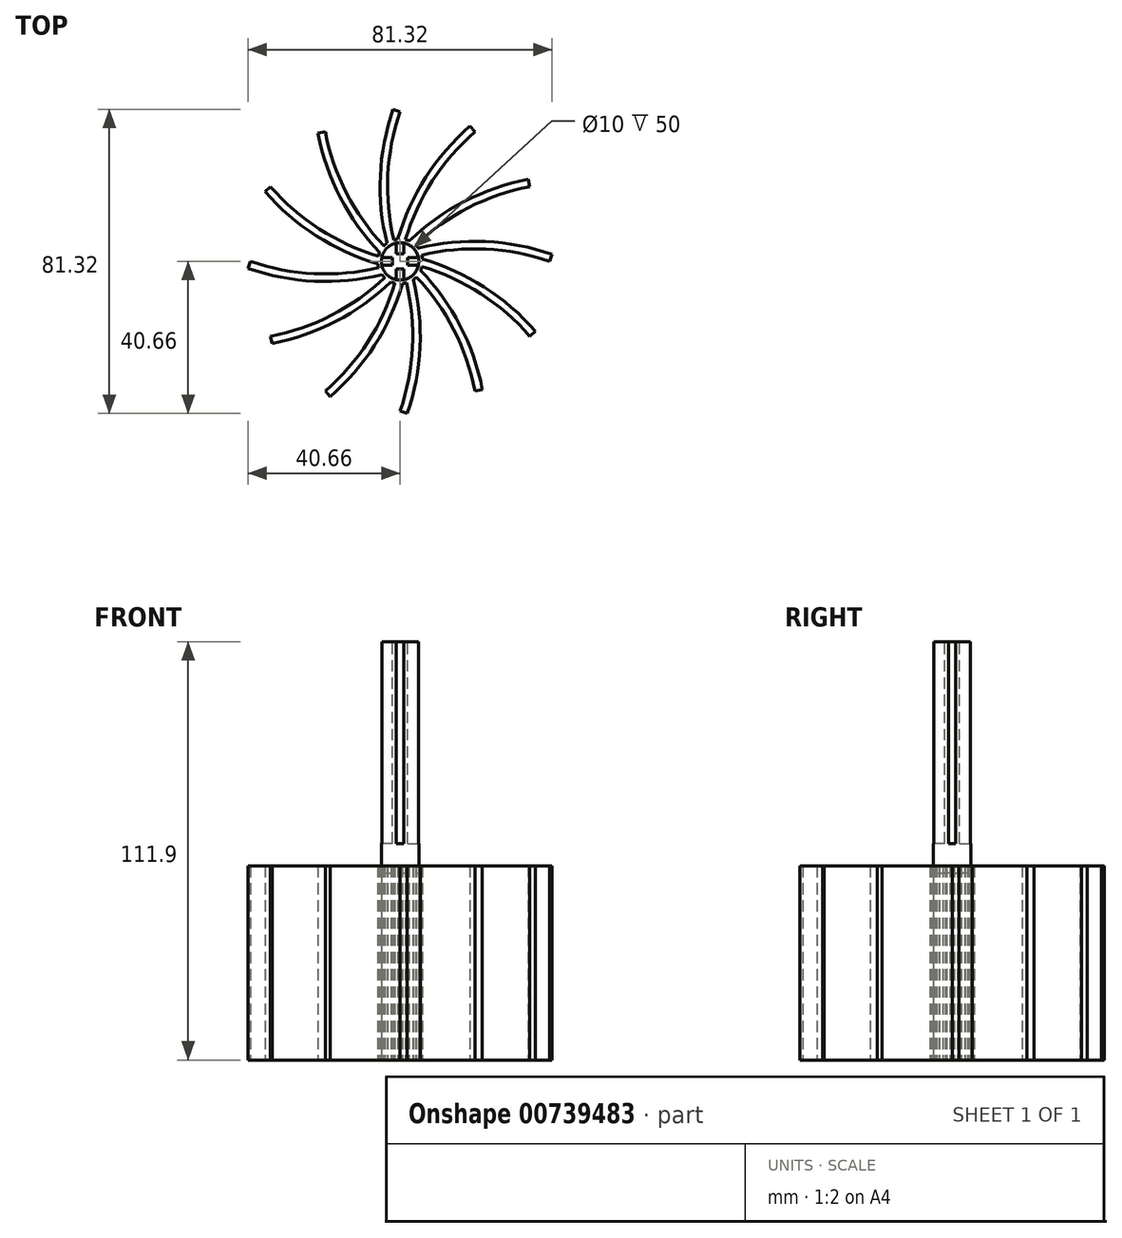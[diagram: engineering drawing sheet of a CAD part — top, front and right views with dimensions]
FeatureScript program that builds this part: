
annotation { "Feature Type Name" : "Feature", "Feature Type Description" : "" }
export const myFeature = defineFeature(function(context is Context, id is Id, definition is map)
    precondition{}
    {
        {
            var Q0;
            Q0=qCreatedBy(makeId("Top.planeOp"),FACE);
            var sketch = newSketch(context, id + "F0", { "sketchPlane" : qUnion([Q0])});
            skCircle(sketch, "E0", {"center": v(0, 0) * mm, "radius": 6 * mm});
            skArc(sketch, "E1", {"start": v(0, 40) * mm, "mid": v(-3.37, 20) * mm, "end": v(0, 0) * mm});
            skArc(sketch, "E2.1.0", {"start": v(-20, 34.64) * mm, "mid": v(-12.92, 15.64) * mm, "end": v(0, 0) * mm});
            skArc(sketch, "E2.2.0", {"start": v(-34.64, 20) * mm, "mid": v(-19, 7.08) * mm, "end": v(0, 0) * mm});
            skArc(sketch, "E2.3.0", {"start": v(-40, 0) * mm, "mid": v(-20, -3.37) * mm, "end": v(0, 0) * mm});
            skArc(sketch, "E2.4.0", {"start": v(-34.64, -20) * mm, "mid": v(-15.64, -12.92) * mm, "end": v(0, 0) * mm});
            skArc(sketch, "E2.5.0", {"start": v(-20, -34.64) * mm, "mid": v(-7.08, -19) * mm, "end": v(0, 0) * mm});
            skArc(sketch, "E2.6.0", {"start": v(0, -40) * mm, "mid": v(3.37, -20) * mm, "end": v(0, 0) * mm});
            skArc(sketch, "E2.7.0", {"start": v(20, -34.64) * mm, "mid": v(12.92, -15.64) * mm, "end": v(0, 0) * mm});
            skArc(sketch, "E2.8.0", {"start": v(34.64, -20) * mm, "mid": v(19, -7.08) * mm, "end": v(0, 0) * mm});
            skArc(sketch, "E2.9.0", {"start": v(40, 0) * mm, "mid": v(20, 3.37) * mm, "end": v(0, 0) * mm});
            skArc(sketch, "E2.10.0", {"start": v(34.64, 20) * mm, "mid": v(15.64, 12.92) * mm, "end": v(0, 0) * mm});
            skArc(sketch, "E2.11.0", {"start": v(20, 34.64) * mm, "mid": v(7.08, 19) * mm, "end": v(0, 0) * mm});
            skArc(sketch, "E3.0", {"start": v(-1.89, 40.66) * mm, "mid": v(-5.37, 20) * mm, "end": v(-1.89, -0.66) * mm});
            skArc(sketch, "E4.0", {"start": v(-21.96, 34.26) * mm, "mid": v(-14.65, 14.64) * mm, "end": v(-1.3, -1.51) * mm});
            skArc(sketch, "E5.0", {"start": v(-36.15, 18.7) * mm, "mid": v(-20, 5.35) * mm, "end": v(-0.38, -1.96) * mm});
            skArc(sketch, "E6.0", {"start": v(-40.66, -1.89) * mm, "mid": v(-20, -5.37) * mm, "end": v(0.66, -1.89) * mm});
            skArc(sketch, "E7.0", {"start": v(-34.26, -21.96) * mm, "mid": v(-14.64, -14.65) * mm, "end": v(1.51, -1.3) * mm});
            skArc(sketch, "E8.0", {"start": v(-18.7, -36.15) * mm, "mid": v(-5.35, -20) * mm, "end": v(1.96, -0.38) * mm});
            skArc(sketch, "E9.0", {"start": v(1.89, -40.66) * mm, "mid": v(5.37, -20) * mm, "end": v(1.89, 0.66) * mm});
            skArc(sketch, "E10.0", {"start": v(21.96, -34.26) * mm, "mid": v(14.65, -14.64) * mm, "end": v(1.3, 1.51) * mm});
            skArc(sketch, "E11.0", {"start": v(36.15, -18.7) * mm, "mid": v(20, -5.35) * mm, "end": v(0.38, 1.96) * mm});
            skArc(sketch, "E12.0", {"start": v(40.66, 1.89) * mm, "mid": v(20, 5.37) * mm, "end": v(-0.66, 1.89) * mm});
            skArc(sketch, "E13.0", {"start": v(34.26, 21.96) * mm, "mid": v(14.64, 14.65) * mm, "end": v(-1.51, 1.3) * mm});
            skArc(sketch, "E14.0", {"start": v(18.7, 36.15) * mm, "mid": v(5.35, 20) * mm, "end": v(-1.96, 0.38) * mm});
            skLineSegment(sketch, "E15", {"start": v(-21.96, 34.26) * mm, "end": v(-20, 34.64) * mm});
            skLineSegment(sketch, "E16", {"start": v(-36.15, 18.7) * mm, "end": v(-34.64, 20) * mm});
            skLineSegment(sketch, "E17", {"start": v(-40.66, -1.89) * mm, "end": v(-40, 0) * mm});
            skLineSegment(sketch, "E18", {"start": v(-34.64, -20) * mm, "end": v(-34.26, -21.96) * mm});
            skLineSegment(sketch, "E19", {"start": v(-20, -34.64) * mm, "end": v(-18.7, -36.15) * mm});
            skLineSegment(sketch, "E20", {"start": v(0, -40) * mm, "end": v(1.89, -40.66) * mm});
            skLineSegment(sketch, "E21", {"start": v(20, -34.64) * mm, "end": v(21.96, -34.26) * mm});
            skLineSegment(sketch, "E22", {"start": v(34.64, -20) * mm, "end": v(36.15, -18.7) * mm});
            skLineSegment(sketch, "E23", {"start": v(40, 0) * mm, "end": v(40.66, 1.89) * mm});
            skLineSegment(sketch, "E24", {"start": v(34.64, 20) * mm, "end": v(34.26, 21.96) * mm});
            skLineSegment(sketch, "E25", {"start": v(20, 34.64) * mm, "end": v(18.7, 36.15) * mm});
            skLineSegment(sketch, "E26", {"start": v(-1.89, 40.66) * mm, "end": v(0, 40) * mm});
            skSolve(sketch);
        }
        {
            var Q0;
            {var subQ0=sQuery(id+"F0.wireOp",EDGE,"E2.10.0");var subQ1=makeQuery(id+"F0.imprint","INTERSECT",VERTEX,{"derivedFrom":[subQ0,sQuery(id+"F0.wireOp",EDGE,"E10.0")]});Q0=makeQuery(id+"F0.imprint","IMPRINT",FACE,{"disambiguationData":[TD([[makeQuery(id+"F0.imprint","IMPRINT",EDGE,{"disambiguationData":[TD([[subQ1,1.0]])],"derivedFrom":subQ0}),-1.0]])]});}
            var Q1;
            {var subQ0=sQuery(id+"F0.wireOp",EDGE,"E2.9.0");var subQ1=makeQuery(id+"F0.imprint","INTERSECT",VERTEX,{"derivedFrom":[subQ0,sQuery(id+"F0.wireOp",EDGE,"E9.0")]});Q1=makeQuery(id+"F0.imprint","IMPRINT",FACE,{"disambiguationData":[TD([[makeQuery(id+"F0.imprint","IMPRINT",EDGE,{"disambiguationData":[TD([[subQ1,1.0]])],"derivedFrom":subQ0}),-1.0]])]});}
            var Q2;
            {var subQ0=sQuery(id+"F0.wireOp",EDGE,"E2.8.0");var subQ1=makeQuery(id+"F0.imprint","INTERSECT",VERTEX,{"derivedFrom":[subQ0,sQuery(id+"F0.wireOp",EDGE,"E8.0")]});Q2=makeQuery(id+"F0.imprint","IMPRINT",FACE,{"disambiguationData":[TD([[makeQuery(id+"F0.imprint","IMPRINT",EDGE,{"disambiguationData":[TD([[subQ1,1.0]])],"derivedFrom":subQ0}),-1.0]])]});}
            var Q3;
            {var subQ0=sQuery(id+"F0.wireOp",EDGE,"E2.7.0");var subQ1=makeQuery(id+"F0.imprint","INTERSECT",VERTEX,{"derivedFrom":[subQ0,sQuery(id+"F0.wireOp",EDGE,"E7.0")]});Q3=makeQuery(id+"F0.imprint","IMPRINT",FACE,{"disambiguationData":[TD([[makeQuery(id+"F0.imprint","IMPRINT",EDGE,{"disambiguationData":[TD([[subQ1,1.0]])],"derivedFrom":subQ0}),-1.0]])]});}
            var Q4;
            {var subQ0=sQuery(id+"F0.wireOp",EDGE,"E2.6.0");var subQ1=makeQuery(id+"F0.imprint","INTERSECT",VERTEX,{"derivedFrom":[subQ0,sQuery(id+"F0.wireOp",EDGE,"E6.0")]});Q4=makeQuery(id+"F0.imprint","IMPRINT",FACE,{"disambiguationData":[TD([[makeQuery(id+"F0.imprint","IMPRINT",EDGE,{"disambiguationData":[TD([[subQ1,1.0]])],"derivedFrom":subQ0}),-1.0]])]});}
            var Q5;
            {var subQ0=sQuery(id+"F0.wireOp",EDGE,"E2.5.0");var subQ1=makeQuery(id+"F0.imprint","INTERSECT",VERTEX,{"derivedFrom":[subQ0,sQuery(id+"F0.wireOp",EDGE,"E5.0")]});Q5=makeQuery(id+"F0.imprint","IMPRINT",FACE,{"disambiguationData":[TD([[makeQuery(id+"F0.imprint","IMPRINT",EDGE,{"disambiguationData":[TD([[subQ1,1.0]])],"derivedFrom":subQ0}),-1.0]])]});}
            var Q6;
            {var subQ0=sQuery(id+"F0.wireOp",EDGE,"E2.4.0");var subQ1=makeQuery(id+"F0.imprint","INTERSECT",VERTEX,{"derivedFrom":[subQ0,sQuery(id+"F0.wireOp",EDGE,"E4.0")]});Q6=makeQuery(id+"F0.imprint","IMPRINT",FACE,{"disambiguationData":[TD([[makeQuery(id+"F0.imprint","IMPRINT",EDGE,{"disambiguationData":[TD([[subQ1,1.0]])],"derivedFrom":subQ0}),-1.0]])]});}
            var Q7;
            {var subQ0=sQuery(id+"F0.wireOp",EDGE,"E2.3.0");var subQ1=makeQuery(id+"F0.imprint","INTERSECT",VERTEX,{"derivedFrom":[subQ0,sQuery(id+"F0.wireOp",EDGE,"E3.0")]});Q7=makeQuery(id+"F0.imprint","IMPRINT",FACE,{"disambiguationData":[TD([[makeQuery(id+"F0.imprint","IMPRINT",EDGE,{"disambiguationData":[TD([[subQ1,1.0]])],"derivedFrom":subQ0}),-1.0]])]});}
            var Q8;
            {var subQ0=sQuery(id+"F0.wireOp",EDGE,"E2.2.0");var subQ1=makeQuery(id+"F0.imprint","INTERSECT",VERTEX,{"derivedFrom":[subQ0,sQuery(id+"F0.wireOp",EDGE,"E14.0")]});Q8=makeQuery(id+"F0.imprint","IMPRINT",FACE,{"disambiguationData":[TD([[makeQuery(id+"F0.imprint","IMPRINT",EDGE,{"disambiguationData":[TD([[subQ1,1.0]])],"derivedFrom":subQ0}),-1.0]])]});}
            var Q9;
            {var subQ0=sQuery(id+"F0.wireOp",EDGE,"E2.1.0");var subQ1=makeQuery(id+"F0.imprint","INTERSECT",VERTEX,{"derivedFrom":[subQ0,sQuery(id+"F0.wireOp",EDGE,"E13.0")]});Q9=makeQuery(id+"F0.imprint","IMPRINT",FACE,{"disambiguationData":[TD([[makeQuery(id+"F0.imprint","IMPRINT",EDGE,{"disambiguationData":[TD([[subQ1,1.0]])],"derivedFrom":subQ0}),-1.0]])]});}
            var Q10;
            {var subQ0=sQuery(id+"F0.wireOp",EDGE,"E1");var subQ1=makeQuery(id+"F0.imprint","INTERSECT",VERTEX,{"derivedFrom":[subQ0,sQuery(id+"F0.wireOp",EDGE,"E12.0")]});Q10=makeQuery(id+"F0.imprint","IMPRINT",FACE,{"disambiguationData":[TD([[makeQuery(id+"F0.imprint","IMPRINT",EDGE,{"disambiguationData":[TD([[subQ1,1.0]])],"derivedFrom":subQ0}),-1.0]])]});}
            var Q11;
            {var subQ0=sQuery(id+"F0.wireOp",EDGE,"E2.11.0");var subQ5=makeQuery(id+"F0.imprint","INTERSECT",VERTEX,{"derivedFrom":[subQ0,sQuery(id+"F0.wireOp",EDGE,"E11.0")]});Q11=makeQuery(id+"F0.imprint","IMPRINT",FACE,{"disambiguationData":[TD([[makeQuery(id+"F0.imprint","IMPRINT",EDGE,{"disambiguationData":[TD([[subQ5,1.0]])],"derivedFrom":subQ0}),-1.0]])]});}
            var Q12;
            {var subQ0=sQuery(id+"F0.wireOp",EDGE,"E12.0");var subQ1=sQuery(id+"F0.wireOp",EDGE,"E1");var subQ2=makeQuery(id+"F0.imprint","INTERSECT",VERTEX,{"derivedFrom":[subQ1,subQ0]});Q12=makeQuery(id+"F0.imprint","IMPRINT",FACE,{"disambiguationData":[TD([[makeQuery(id+"F0.imprint","IMPRINT",EDGE,{"disambiguationData":[TD([[subQ2,1.0]])],"derivedFrom":subQ1}),1.0]])]});}
            var Q13;
            {var subQ0=sQuery(id+"F0.wireOp",EDGE,"E12.0");var subQ1=sQuery(id+"F0.wireOp",EDGE,"E2.10.0");var subQ2=makeQuery(id+"F0.imprint","INTERSECT",VERTEX,{"derivedFrom":[subQ1,subQ0]});Q13=makeQuery(id+"F0.imprint","IMPRINT",FACE,{"disambiguationData":[TD([[makeQuery(id+"F0.imprint","IMPRINT",EDGE,{"disambiguationData":[TD([[subQ2,-1.0]])],"derivedFrom":subQ1}),-1.0]])]});}
            var Q14;
            {var subQ0=sQuery(id+"F0.wireOp",EDGE,"E11.0");var subQ1=sQuery(id+"F0.wireOp",EDGE,"E2.9.0");var subQ2=makeQuery(id+"F0.imprint","INTERSECT",VERTEX,{"derivedFrom":[subQ1,subQ0]});Q14=makeQuery(id+"F0.imprint","IMPRINT",FACE,{"disambiguationData":[TD([[makeQuery(id+"F0.imprint","IMPRINT",EDGE,{"disambiguationData":[TD([[subQ2,-1.0]])],"derivedFrom":subQ1}),-1.0]])]});}
            var Q15;
            {var subQ5=sQuery(id+"F0.wireOp",EDGE,"E11.0");var subQ7=sQuery(id+"F0.wireOp",EDGE,"E0");var subQ9=makeQuery(id+"F0.imprint","INTERSECT",VERTEX,{"derivedFrom":[subQ7,subQ5]});Q15=makeQuery(id+"F0.imprint","IMPRINT",FACE,{"disambiguationData":[TD([[makeQuery(id+"F0.imprint","IMPRINT",EDGE,{"disambiguationData":[TD([[subQ9,1.0]])],"derivedFrom":subQ7}),1.0]])]});}
            var Q16;
            {var subQ0=sQuery(id+"F0.wireOp",EDGE,"E10.0");var subQ1=sQuery(id+"F0.wireOp",EDGE,"E2.8.0");var subQ2=makeQuery(id+"F0.imprint","INTERSECT",VERTEX,{"derivedFrom":[subQ1,subQ0]});Q16=makeQuery(id+"F0.imprint","IMPRINT",FACE,{"disambiguationData":[TD([[makeQuery(id+"F0.imprint","IMPRINT",EDGE,{"disambiguationData":[TD([[subQ2,-1.0]])],"derivedFrom":subQ1}),-1.0]])]});}
            var Q17;
            {var subQ1=sQuery(id+"F0.wireOp",EDGE,"E2.9.0");var subQ5=sQuery(id+"F0.wireOp",EDGE,"E0");var subQ6=makeQuery(id+"F0.imprint","INTERSECT",VERTEX,{"derivedFrom":[subQ5,subQ1]});Q17=makeQuery(id+"F0.imprint","IMPRINT",FACE,{"disambiguationData":[TD([[makeQuery(id+"F0.imprint","IMPRINT",EDGE,{"disambiguationData":[TD([[subQ6,-1.0]])],"derivedFrom":subQ5}),1.0]])]});}
            var Q18;
            {var subQ1=sQuery(id+"F0.wireOp",EDGE,"E2.10.0");var subQ7=sQuery(id+"F0.wireOp",EDGE,"E0");var subQ9=makeQuery(id+"F0.imprint","INTERSECT",VERTEX,{"derivedFrom":[subQ7,subQ1]});Q18=makeQuery(id+"F0.imprint","IMPRINT",FACE,{"disambiguationData":[TD([[makeQuery(id+"F0.imprint","IMPRINT",EDGE,{"disambiguationData":[TD([[subQ9,-1.0]])],"derivedFrom":subQ7}),1.0]])]});}
            var Q19;
            {var subQ1=sQuery(id+"F0.wireOp",EDGE,"E2.7.0");var subQ7=sQuery(id+"F0.wireOp",EDGE,"E0");var subQ8=makeQuery(id+"F0.imprint","INTERSECT",VERTEX,{"derivedFrom":[subQ7,subQ1]});Q19=makeQuery(id+"F0.imprint","IMPRINT",FACE,{"disambiguationData":[TD([[makeQuery(id+"F0.imprint","IMPRINT",EDGE,{"disambiguationData":[TD([[subQ8,-1.0]])],"derivedFrom":subQ7}),1.0]])]});}
            var Q20;
            {var subQ0=sQuery(id+"F0.wireOp",EDGE,"E9.0");var subQ1=sQuery(id+"F0.wireOp",EDGE,"E2.7.0");var subQ2=makeQuery(id+"F0.imprint","INTERSECT",VERTEX,{"derivedFrom":[subQ1,subQ0]});Q20=makeQuery(id+"F0.imprint","IMPRINT",FACE,{"disambiguationData":[TD([[makeQuery(id+"F0.imprint","IMPRINT",EDGE,{"disambiguationData":[TD([[subQ2,-1.0]])],"derivedFrom":subQ1}),-1.0]])]});}
            var Q21;
            {var subQ1=sQuery(id+"F0.wireOp",EDGE,"E2.6.0");var subQ7=sQuery(id+"F0.wireOp",EDGE,"E0");var subQ8=makeQuery(id+"F0.imprint","INTERSECT",VERTEX,{"derivedFrom":[subQ7,subQ1]});Q21=makeQuery(id+"F0.imprint","IMPRINT",FACE,{"disambiguationData":[TD([[makeQuery(id+"F0.imprint","IMPRINT",EDGE,{"disambiguationData":[TD([[subQ8,-1.0]])],"derivedFrom":subQ7}),1.0]])]});}
            var Q22;
            {var subQ0=sQuery(id+"F0.wireOp",EDGE,"E8.0");var subQ1=sQuery(id+"F0.wireOp",EDGE,"E2.6.0");var subQ2=makeQuery(id+"F0.imprint","INTERSECT",VERTEX,{"derivedFrom":[subQ1,subQ0]});Q22=makeQuery(id+"F0.imprint","IMPRINT",FACE,{"disambiguationData":[TD([[makeQuery(id+"F0.imprint","IMPRINT",EDGE,{"disambiguationData":[TD([[subQ2,-1.0]])],"derivedFrom":subQ1}),-1.0]])]});}
            var Q23;
            {var subQ5=sQuery(id+"F0.wireOp",EDGE,"E2.5.0");var subQ6=sQuery(id+"F0.wireOp",EDGE,"E0");var subQ7=makeQuery(id+"F0.imprint","INTERSECT",VERTEX,{"derivedFrom":[subQ6,subQ5]});Q23=makeQuery(id+"F0.imprint","IMPRINT",FACE,{"disambiguationData":[TD([[makeQuery(id+"F0.imprint","IMPRINT",EDGE,{"disambiguationData":[TD([[subQ7,-1.0]])],"derivedFrom":subQ6}),1.0]])]});}
            var Q24;
            {var subQ0=sQuery(id+"F0.wireOp",EDGE,"E7.0");var subQ1=sQuery(id+"F0.wireOp",EDGE,"E2.5.0");var subQ2=makeQuery(id+"F0.imprint","INTERSECT",VERTEX,{"derivedFrom":[subQ1,subQ0]});Q24=makeQuery(id+"F0.imprint","IMPRINT",FACE,{"disambiguationData":[TD([[makeQuery(id+"F0.imprint","IMPRINT",EDGE,{"disambiguationData":[TD([[subQ2,-1.0]])],"derivedFrom":subQ1}),-1.0]])]});}
            var Q25;
            {var subQ1=sQuery(id+"F0.wireOp",EDGE,"E2.4.0");var subQ7=sQuery(id+"F0.wireOp",EDGE,"E0");var subQ8=makeQuery(id+"F0.imprint","INTERSECT",VERTEX,{"derivedFrom":[subQ7,subQ1]});Q25=makeQuery(id+"F0.imprint","IMPRINT",FACE,{"disambiguationData":[TD([[makeQuery(id+"F0.imprint","IMPRINT",EDGE,{"disambiguationData":[TD([[subQ8,-1.0]])],"derivedFrom":subQ7}),1.0]])]});}
            var Q26;
            {var subQ0=sQuery(id+"F0.wireOp",EDGE,"E6.0");var subQ1=sQuery(id+"F0.wireOp",EDGE,"E2.4.0");var subQ2=makeQuery(id+"F0.imprint","INTERSECT",VERTEX,{"derivedFrom":[subQ1,subQ0]});Q26=makeQuery(id+"F0.imprint","IMPRINT",FACE,{"disambiguationData":[TD([[makeQuery(id+"F0.imprint","IMPRINT",EDGE,{"disambiguationData":[TD([[subQ2,-1.0]])],"derivedFrom":subQ1}),-1.0]])]});}
            var Q27;
            {var subQ1=sQuery(id+"F0.wireOp",EDGE,"E2.3.0");var subQ7=sQuery(id+"F0.wireOp",EDGE,"E0");var subQ8=makeQuery(id+"F0.imprint","INTERSECT",VERTEX,{"derivedFrom":[subQ7,subQ1]});Q27=makeQuery(id+"F0.imprint","IMPRINT",FACE,{"disambiguationData":[TD([[makeQuery(id+"F0.imprint","IMPRINT",EDGE,{"disambiguationData":[TD([[subQ8,-1.0]])],"derivedFrom":subQ7}),1.0]])]});}
            var Q28;
            {var subQ0=sQuery(id+"F0.wireOp",EDGE,"E5.0");var subQ1=sQuery(id+"F0.wireOp",EDGE,"E2.3.0");var subQ2=makeQuery(id+"F0.imprint","INTERSECT",VERTEX,{"derivedFrom":[subQ1,subQ0]});Q28=makeQuery(id+"F0.imprint","IMPRINT",FACE,{"disambiguationData":[TD([[makeQuery(id+"F0.imprint","IMPRINT",EDGE,{"disambiguationData":[TD([[subQ2,-1.0]])],"derivedFrom":subQ1}),-1.0]])]});}
            var Q29;
            {var subQ1=sQuery(id+"F0.wireOp",EDGE,"E2.2.0");var subQ5=sQuery(id+"F0.wireOp",EDGE,"E0");var subQ6=makeQuery(id+"F0.imprint","INTERSECT",VERTEX,{"derivedFrom":[subQ5,subQ1]});Q29=makeQuery(id+"F0.imprint","IMPRINT",FACE,{"disambiguationData":[TD([[makeQuery(id+"F0.imprint","IMPRINT",EDGE,{"disambiguationData":[TD([[subQ6,-1.0]])],"derivedFrom":subQ5}),1.0]])]});}
            var Q30;
            {var subQ0=sQuery(id+"F0.wireOp",EDGE,"E4.0");var subQ1=sQuery(id+"F0.wireOp",EDGE,"E2.2.0");var subQ2=makeQuery(id+"F0.imprint","INTERSECT",VERTEX,{"derivedFrom":[subQ1,subQ0]});Q30=makeQuery(id+"F0.imprint","IMPRINT",FACE,{"disambiguationData":[TD([[makeQuery(id+"F0.imprint","IMPRINT",EDGE,{"disambiguationData":[TD([[subQ2,-1.0]])],"derivedFrom":subQ1}),-1.0]])]});}
            var Q31;
            {var subQ1=sQuery(id+"F0.wireOp",EDGE,"E2.1.0");var subQ5=sQuery(id+"F0.wireOp",EDGE,"E0");var subQ6=makeQuery(id+"F0.imprint","INTERSECT",VERTEX,{"derivedFrom":[subQ5,subQ1]});Q31=makeQuery(id+"F0.imprint","IMPRINT",FACE,{"disambiguationData":[TD([[makeQuery(id+"F0.imprint","IMPRINT",EDGE,{"disambiguationData":[TD([[subQ6,-1.0]])],"derivedFrom":subQ5}),1.0]])]});}
            var Q32;
            {var subQ0=sQuery(id+"F0.wireOp",EDGE,"E3.0");var subQ1=sQuery(id+"F0.wireOp",EDGE,"E2.1.0");var subQ2=makeQuery(id+"F0.imprint","INTERSECT",VERTEX,{"derivedFrom":[subQ1,subQ0]});Q32=makeQuery(id+"F0.imprint","IMPRINT",FACE,{"disambiguationData":[TD([[makeQuery(id+"F0.imprint","IMPRINT",EDGE,{"disambiguationData":[TD([[subQ2,-1.0]])],"derivedFrom":subQ1}),-1.0]])]});}
            var Q33;
            {var subQ5=sQuery(id+"F0.wireOp",EDGE,"E1");var subQ7=sQuery(id+"F0.wireOp",EDGE,"E0");var subQ9=makeQuery(id+"F0.imprint","INTERSECT",VERTEX,{"derivedFrom":[subQ7,subQ5]});Q33=makeQuery(id+"F0.imprint","IMPRINT",FACE,{"disambiguationData":[TD([[makeQuery(id+"F0.imprint","IMPRINT",EDGE,{"disambiguationData":[TD([[subQ9,-1.0]])],"derivedFrom":subQ7}),1.0]])]});}
            var Q34;
            {var subQ0=sQuery(id+"F0.wireOp",EDGE,"E14.0");var subQ1=sQuery(id+"F0.wireOp",EDGE,"E1");var subQ2=makeQuery(id+"F0.imprint","INTERSECT",VERTEX,{"derivedFrom":[subQ1,subQ0]});Q34=makeQuery(id+"F0.imprint","IMPRINT",FACE,{"disambiguationData":[TD([[makeQuery(id+"F0.imprint","IMPRINT",EDGE,{"disambiguationData":[TD([[subQ2,-1.0]])],"derivedFrom":subQ1}),-1.0]])]});}
            var Q35;
            {var subQ3=sQuery(id+"F0.wireOp",EDGE,"E2.11.0");var subQ5=sQuery(id+"F0.wireOp",EDGE,"E0");var subQ6=makeQuery(id+"F0.imprint","INTERSECT",VERTEX,{"derivedFrom":[subQ5,subQ3]});Q35=makeQuery(id+"F0.imprint","IMPRINT",FACE,{"disambiguationData":[TD([[makeQuery(id+"F0.imprint","IMPRINT",EDGE,{"disambiguationData":[TD([[subQ6,-1.0]])],"derivedFrom":subQ5}),1.0]])]});}
            var Q36;
            {var subQ0=sQuery(id+"F0.wireOp",EDGE,"E13.0");var subQ1=sQuery(id+"F0.wireOp",EDGE,"E0");var subQ2=makeQuery(id+"F0.imprint","INTERSECT",VERTEX,{"derivedFrom":[subQ1,subQ0]});Q36=makeQuery(id+"F0.imprint","IMPRINT",FACE,{"disambiguationData":[TD([[makeQuery(id+"F0.imprint","IMPRINT",EDGE,{"disambiguationData":[TD([[subQ2,-1.0]])],"derivedFrom":subQ1}),1.0]])]});}
            var Q37;
            {var subQ0=sQuery(id+"F0.wireOp",EDGE,"E12.0");var subQ1=sQuery(id+"F0.wireOp",EDGE,"E0");var subQ2=makeQuery(id+"F0.imprint","INTERSECT",VERTEX,{"derivedFrom":[subQ1,subQ0]});Q37=makeQuery(id+"F0.imprint","IMPRINT",FACE,{"disambiguationData":[TD([[makeQuery(id+"F0.imprint","IMPRINT",EDGE,{"disambiguationData":[TD([[subQ2,-1.0]])],"derivedFrom":subQ1}),1.0]])]});}
            var Q38;
            {var subQ0=sQuery(id+"F0.wireOp",EDGE,"E2.9.0");var subQ1=sQuery(id+"F0.wireOp",EDGE,"E0");var subQ2=makeQuery(id+"F0.imprint","INTERSECT",VERTEX,{"derivedFrom":[subQ1,subQ0]});Q38=makeQuery(id+"F0.imprint","IMPRINT",FACE,{"disambiguationData":[TD([[makeQuery(id+"F0.imprint","IMPRINT",EDGE,{"disambiguationData":[TD([[subQ2,1.0]])],"derivedFrom":subQ1}),1.0]])]});}
            var Q39;
            {var subQ0=sQuery(id+"F0.wireOp",EDGE,"E10.0");var subQ1=sQuery(id+"F0.wireOp",EDGE,"E0");var subQ2=makeQuery(id+"F0.imprint","INTERSECT",VERTEX,{"derivedFrom":[subQ1,subQ0]});Q39=makeQuery(id+"F0.imprint","IMPRINT",FACE,{"disambiguationData":[TD([[makeQuery(id+"F0.imprint","IMPRINT",EDGE,{"disambiguationData":[TD([[subQ2,-1.0]])],"derivedFrom":subQ1}),1.0]])]});}
            var Q40;
            {var subQ0=sQuery(id+"F0.wireOp",EDGE,"E9.0");var subQ1=sQuery(id+"F0.wireOp",EDGE,"E0");var subQ2=makeQuery(id+"F0.imprint","INTERSECT",VERTEX,{"derivedFrom":[subQ1,subQ0]});Q40=makeQuery(id+"F0.imprint","IMPRINT",FACE,{"disambiguationData":[TD([[makeQuery(id+"F0.imprint","IMPRINT",EDGE,{"disambiguationData":[TD([[subQ2,-1.0]])],"derivedFrom":subQ1}),1.0]])]});}
            var Q41;
            {var subQ0=sQuery(id+"F0.wireOp",EDGE,"E8.0");var subQ1=sQuery(id+"F0.wireOp",EDGE,"E0");var subQ2=makeQuery(id+"F0.imprint","INTERSECT",VERTEX,{"derivedFrom":[subQ1,subQ0]});Q41=makeQuery(id+"F0.imprint","IMPRINT",FACE,{"disambiguationData":[TD([[makeQuery(id+"F0.imprint","IMPRINT",EDGE,{"disambiguationData":[TD([[subQ2,-1.0]])],"derivedFrom":subQ1}),1.0]])]});}
            var Q42;
            {var subQ0=sQuery(id+"F0.wireOp",EDGE,"E7.0");var subQ1=sQuery(id+"F0.wireOp",EDGE,"E0");var subQ2=makeQuery(id+"F0.imprint","INTERSECT",VERTEX,{"derivedFrom":[subQ1,subQ0]});Q42=makeQuery(id+"F0.imprint","IMPRINT",FACE,{"disambiguationData":[TD([[makeQuery(id+"F0.imprint","IMPRINT",EDGE,{"disambiguationData":[TD([[subQ2,-1.0]])],"derivedFrom":subQ1}),1.0]])]});}
            var Q43;
            {var subQ0=sQuery(id+"F0.wireOp",EDGE,"E6.0");var subQ1=sQuery(id+"F0.wireOp",EDGE,"E0");var subQ2=makeQuery(id+"F0.imprint","INTERSECT",VERTEX,{"derivedFrom":[subQ1,subQ0]});Q43=makeQuery(id+"F0.imprint","IMPRINT",FACE,{"disambiguationData":[TD([[makeQuery(id+"F0.imprint","IMPRINT",EDGE,{"disambiguationData":[TD([[subQ2,-1.0]])],"derivedFrom":subQ1}),1.0]])]});}
            var Q44;
            {var subQ0=sQuery(id+"F0.wireOp",EDGE,"E5.0");var subQ1=sQuery(id+"F0.wireOp",EDGE,"E0");var subQ2=makeQuery(id+"F0.imprint","INTERSECT",VERTEX,{"derivedFrom":[subQ1,subQ0]});Q44=makeQuery(id+"F0.imprint","IMPRINT",FACE,{"disambiguationData":[TD([[makeQuery(id+"F0.imprint","IMPRINT",EDGE,{"disambiguationData":[TD([[subQ2,-1.0]])],"derivedFrom":subQ1}),1.0]])]});}
            var Q45;
            {var subQ0=sQuery(id+"F0.wireOp",EDGE,"E4.0");var subQ1=sQuery(id+"F0.wireOp",EDGE,"E0");var subQ2=makeQuery(id+"F0.imprint","INTERSECT",VERTEX,{"derivedFrom":[subQ1,subQ0]});Q45=makeQuery(id+"F0.imprint","IMPRINT",FACE,{"disambiguationData":[TD([[makeQuery(id+"F0.imprint","IMPRINT",EDGE,{"disambiguationData":[TD([[subQ2,-1.0]])],"derivedFrom":subQ1}),1.0]])]});}
            var Q46;
            {var subQ0=sQuery(id+"F0.wireOp",EDGE,"E3.0");var subQ1=sQuery(id+"F0.wireOp",EDGE,"E0");var subQ2=makeQuery(id+"F0.imprint","INTERSECT",VERTEX,{"derivedFrom":[subQ1,subQ0]});Q46=makeQuery(id+"F0.imprint","IMPRINT",FACE,{"disambiguationData":[TD([[makeQuery(id+"F0.imprint","IMPRINT",EDGE,{"disambiguationData":[TD([[subQ2,-1.0]])],"derivedFrom":subQ1}),1.0]])]});}
            var Q47;
            {var subQ0=sQuery(id+"F0.wireOp",EDGE,"E14.0");var subQ1=sQuery(id+"F0.wireOp",EDGE,"E0");var subQ2=makeQuery(id+"F0.imprint","INTERSECT",VERTEX,{"derivedFrom":[subQ1,subQ0]});Q47=makeQuery(id+"F0.imprint","IMPRINT",FACE,{"disambiguationData":[TD([[makeQuery(id+"F0.imprint","IMPRINT",EDGE,{"disambiguationData":[TD([[subQ2,-1.0]])],"derivedFrom":subQ1}),1.0]])]});}
            var Q48;
            {var subQ5=sQuery(id+"F0.wireOp",EDGE,"E26");Q48=makeQuery(id+"F0.imprint","IMPRINT",FACE,{"disambiguationData":[TD([[makeQuery(id+"F0.imprint","IMPRINT",EDGE,{"derivedFrom":subQ5}),-1.0]])]});}
            var Q49;
            {var subQ5=sQuery(id+"F0.wireOp",EDGE,"E25");Q49=makeQuery(id+"F0.imprint","IMPRINT",FACE,{"disambiguationData":[TD([[makeQuery(id+"F0.imprint","IMPRINT",EDGE,{"derivedFrom":subQ5}),1.0]])]});}
            var Q50;
            {var subQ5=sQuery(id+"F0.wireOp",EDGE,"E24");Q50=makeQuery(id+"F0.imprint","IMPRINT",FACE,{"disambiguationData":[TD([[makeQuery(id+"F0.imprint","IMPRINT",EDGE,{"derivedFrom":subQ5}),1.0]])]});}
            var Q51;
            {var subQ5=sQuery(id+"F0.wireOp",EDGE,"E23");Q51=makeQuery(id+"F0.imprint","IMPRINT",FACE,{"disambiguationData":[TD([[makeQuery(id+"F0.imprint","IMPRINT",EDGE,{"derivedFrom":subQ5}),1.0]])]});}
            var Q52;
            {var subQ5=sQuery(id+"F0.wireOp",EDGE,"E22");Q52=makeQuery(id+"F0.imprint","IMPRINT",FACE,{"disambiguationData":[TD([[makeQuery(id+"F0.imprint","IMPRINT",EDGE,{"derivedFrom":subQ5}),1.0]])]});}
            var Q53;
            {var subQ5=sQuery(id+"F0.wireOp",EDGE,"E20");Q53=makeQuery(id+"F0.imprint","IMPRINT",FACE,{"disambiguationData":[TD([[makeQuery(id+"F0.imprint","IMPRINT",EDGE,{"derivedFrom":subQ5}),1.0]])]});}
            var Q54;
            {var subQ5=sQuery(id+"F0.wireOp",EDGE,"E19");Q54=makeQuery(id+"F0.imprint","IMPRINT",FACE,{"disambiguationData":[TD([[makeQuery(id+"F0.imprint","IMPRINT",EDGE,{"derivedFrom":subQ5}),1.0]])]});}
            var Q55;
            {var subQ5=sQuery(id+"F0.wireOp",EDGE,"E18");Q55=makeQuery(id+"F0.imprint","IMPRINT",FACE,{"disambiguationData":[TD([[makeQuery(id+"F0.imprint","IMPRINT",EDGE,{"derivedFrom":subQ5}),1.0]])]});}
            var Q56;
            {var subQ5=sQuery(id+"F0.wireOp",EDGE,"E15");Q56=makeQuery(id+"F0.imprint","IMPRINT",FACE,{"disambiguationData":[TD([[makeQuery(id+"F0.imprint","IMPRINT",EDGE,{"derivedFrom":subQ5}),-1.0]])]});}
            var Q57;
            {var subQ5=sQuery(id+"F0.wireOp",EDGE,"E21");Q57=makeQuery(id+"F0.imprint","IMPRINT",FACE,{"disambiguationData":[TD([[makeQuery(id+"F0.imprint","IMPRINT",EDGE,{"derivedFrom":subQ5}),1.0]])]});}
            var Q58;
            {var subQ5=sQuery(id+"F0.wireOp",EDGE,"E17");Q58=makeQuery(id+"F0.imprint","IMPRINT",FACE,{"disambiguationData":[TD([[makeQuery(id+"F0.imprint","IMPRINT",EDGE,{"derivedFrom":subQ5}),-1.0]])]});}
            var Q59;
            {var subQ5=sQuery(id+"F0.wireOp",EDGE,"E16");Q59=makeQuery(id+"F0.imprint","IMPRINT",FACE,{"disambiguationData":[TD([[makeQuery(id+"F0.imprint","IMPRINT",EDGE,{"derivedFrom":subQ5}),-1.0]])]});}
            extrude(context, id + "F1", {"entities" : qUnion([Q0, Q1, Q2, Q3, Q4, Q5, Q6, Q7, Q8, Q9, Q10, Q11, Q12, Q13, Q14, Q15, Q16, Q17, Q18, Q19, Q20, Q21, Q22, Q23, Q24, Q25, Q26, Q27, Q28, Q29, Q30, Q31, Q32, Q33, Q34, Q35, Q36, Q37, Q38, Q39, Q40, Q41, Q42, Q43, Q44, Q45, Q46, Q47, Q48, Q49, Q50, Q51, Q52, Q53, Q54, Q55, Q56, Q57, Q58, Q59]), "depth" : 51.9 * mm, "offsetDistance" : 25 * mm});
        }
        {
            var Q0;
            Q0=makeQuery(id+"F1.opExtrude","CAP_FACE",FACE,{"disambiguationData":[OSD([sQuery(id+"F0.wireOp",EDGE,"E0"),sQuery(id+"F0.wireOp",EDGE,"E1"),sQuery(id+"F0.wireOp",EDGE,"E2.1.0"),sQuery(id+"F0.wireOp",EDGE,"E2.2.0"),sQuery(id+"F0.wireOp",EDGE,"E2.3.0"),sQuery(id+"F0.wireOp",EDGE,"E2.4.0"),sQuery(id+"F0.wireOp",EDGE,"E2.5.0"),sQuery(id+"F0.wireOp",EDGE,"E2.6.0"),sQuery(id+"F0.wireOp",EDGE,"E2.7.0"),sQuery(id+"F0.wireOp",EDGE,"E2.8.0"),sQuery(id+"F0.wireOp",EDGE,"E2.9.0"),sQuery(id+"F0.wireOp",EDGE,"E2.10.0"),sQuery(id+"F0.wireOp",EDGE,"E2.11.0"),sQuery(id+"F0.wireOp",EDGE,"E3.0"),sQuery(id+"F0.wireOp",EDGE,"E4.0"),sQuery(id+"F0.wireOp",EDGE,"E5.0"),sQuery(id+"F0.wireOp",EDGE,"E6.0"),sQuery(id+"F0.wireOp",EDGE,"E7.0"),sQuery(id+"F0.wireOp",EDGE,"E8.0"),sQuery(id+"F0.wireOp",EDGE,"E9.0"),sQuery(id+"F0.wireOp",EDGE,"E10.0"),sQuery(id+"F0.wireOp",EDGE,"E11.0"),sQuery(id+"F0.wireOp",EDGE,"E12.0"),sQuery(id+"F0.wireOp",EDGE,"E13.0"),sQuery(id+"F0.wireOp",EDGE,"E14.0"),sQuery(id+"F0.wireOp",EDGE,"E15"),sQuery(id+"F0.wireOp",EDGE,"E16"),sQuery(id+"F0.wireOp",EDGE,"E17"),sQuery(id+"F0.wireOp",EDGE,"E18"),sQuery(id+"F0.wireOp",EDGE,"E19"),sQuery(id+"F0.wireOp",EDGE,"E20"),sQuery(id+"F0.wireOp",EDGE,"E21"),sQuery(id+"F0.wireOp",EDGE,"E22"),sQuery(id+"F0.wireOp",EDGE,"E23"),sQuery(id+"F0.wireOp",EDGE,"E24"),sQuery(id+"F0.wireOp",EDGE,"E25"),sQuery(id+"F0.wireOp",EDGE,"E26")])],"isStart":true});
            var sketch = newSketch(context, id + "F2", { "sketchPlane" : qUnion([Q0])});
            skCircle(sketch, "E27", {"center": v(0, 0) * mm, "radius": 5 * mm});
            skSolve(sketch);
        }
        {
            var Q0;
            Q0=makeQuery(id+"F2.imprint","IMPRINT",FACE,{"disambiguationData":[TD([[makeQuery(id+"F2.imprint","IMPRINT",EDGE,{"derivedFrom":sQuery(id+"F2.wireOp",EDGE,"E27")}),1.0]])]});
            extrude(context, id + "F3", {"entities" : qUnion([Q0]), "operationType" : NewBodyOperationType.REMOVE, "oppositeDirection" : true, "depth" : 50 * mm, "offsetDistance" : 25 * mm});
        }
        {
            var Q0;
            Q0=makeQuery(id+"F1.opExtrude","CAP_FACE",FACE,{"disambiguationData":[OSD([sQuery(id+"F0.wireOp",EDGE,"E0"),sQuery(id+"F0.wireOp",EDGE,"E1"),sQuery(id+"F0.wireOp",EDGE,"E2.1.0"),sQuery(id+"F0.wireOp",EDGE,"E2.2.0"),sQuery(id+"F0.wireOp",EDGE,"E2.3.0"),sQuery(id+"F0.wireOp",EDGE,"E2.4.0"),sQuery(id+"F0.wireOp",EDGE,"E2.5.0"),sQuery(id+"F0.wireOp",EDGE,"E2.6.0"),sQuery(id+"F0.wireOp",EDGE,"E2.7.0"),sQuery(id+"F0.wireOp",EDGE,"E2.8.0"),sQuery(id+"F0.wireOp",EDGE,"E2.9.0"),sQuery(id+"F0.wireOp",EDGE,"E2.10.0"),sQuery(id+"F0.wireOp",EDGE,"E2.11.0"),sQuery(id+"F0.wireOp",EDGE,"E3.0"),sQuery(id+"F0.wireOp",EDGE,"E4.0"),sQuery(id+"F0.wireOp",EDGE,"E5.0"),sQuery(id+"F0.wireOp",EDGE,"E6.0"),sQuery(id+"F0.wireOp",EDGE,"E7.0"),sQuery(id+"F0.wireOp",EDGE,"E8.0"),sQuery(id+"F0.wireOp",EDGE,"E9.0"),sQuery(id+"F0.wireOp",EDGE,"E10.0"),sQuery(id+"F0.wireOp",EDGE,"E11.0"),sQuery(id+"F0.wireOp",EDGE,"E12.0"),sQuery(id+"F0.wireOp",EDGE,"E13.0"),sQuery(id+"F0.wireOp",EDGE,"E14.0"),sQuery(id+"F0.wireOp",EDGE,"E15"),sQuery(id+"F0.wireOp",EDGE,"E16"),sQuery(id+"F0.wireOp",EDGE,"E17"),sQuery(id+"F0.wireOp",EDGE,"E18"),sQuery(id+"F0.wireOp",EDGE,"E19"),sQuery(id+"F0.wireOp",EDGE,"E20"),sQuery(id+"F0.wireOp",EDGE,"E21"),sQuery(id+"F0.wireOp",EDGE,"E22"),sQuery(id+"F0.wireOp",EDGE,"E23"),sQuery(id+"F0.wireOp",EDGE,"E24"),sQuery(id+"F0.wireOp",EDGE,"E25"),sQuery(id+"F0.wireOp",EDGE,"E26")])],"isStart":false});
            var sketch = newSketch(context, id + "F4", { "sketchPlane" : qUnion([Q0])});
            skCircle(sketch, "E28", {"center": v(0, 0) * mm, "radius": 5 * mm});
            skSolve(sketch);
        }
        {
            var Q0;
            Q0 = qSketchRegion(id + "F4", true);
            extrude(context, id + "F5", {"entities" : qUnion([Q0]), "operationType" : NewBodyOperationType.ADD, "depth" : 60 * mm, "offsetDistance" : 25 * mm});
        }
        {
            var Q0;
            Q0=makeQuery(id+"F5.opExtrude","CAP_FACE",FACE,{"disambiguationData":[OSD([sQuery(id+"F4.wireOp",EDGE,"E28")])],"isStart":false});
            var sketch = newSketch(context, id + "F6", { "sketchPlane" : qUnion([Q0])});
            skLineSegment(sketch, "E29", {"start": v(-1, 2) * mm, "end": v(1, 2) * mm});
            skLineSegment(sketch, "E30", {"start": v(-1, 2) * mm, "end": v(-1, 4.9) * mm});
            skLineSegment(sketch, "E31", {"start": v(1, 2) * mm, "end": v(1, 4.9) * mm});
            skLineSegment(sketch, "E32.1.0", {"start": v(-2, -1) * mm, "end": v(-4.9, -1) * mm});
            skLineSegment(sketch, "E32.1.1", {"start": v(-2, -1) * mm, "end": v(-2, 1) * mm});
            skLineSegment(sketch, "E32.1.2", {"start": v(-2, 1) * mm, "end": v(-4.9, 1) * mm});
            skLineSegment(sketch, "E32.2.0", {"start": v(1, -2) * mm, "end": v(1, -4.9) * mm});
            skLineSegment(sketch, "E32.2.1", {"start": v(1, -2) * mm, "end": v(-1, -2) * mm});
            skLineSegment(sketch, "E32.2.2", {"start": v(-1, -2) * mm, "end": v(-1, -4.9) * mm});
            skLineSegment(sketch, "E32.3.0", {"start": v(2, 1) * mm, "end": v(4.9, 1) * mm});
            skLineSegment(sketch, "E32.3.1", {"start": v(2, 1) * mm, "end": v(2, -1) * mm});
            skLineSegment(sketch, "E32.3.2", {"start": v(2, -1) * mm, "end": v(4.9, -1) * mm});
            skPoint(sketch, "E32.center", {"position": v(0, 0) * mm});
            skSolve(sketch);
        }
        {
            var Q0;
            Q0=makeQuery(id+"F6.imprint","IMPRINT",FACE,{"disambiguationData":[TD([[makeQuery(id+"F6.imprint","IMPRINT",EDGE,{"derivedFrom":sQuery(id+"F6.wireOp",EDGE,"E29")}),1.0]])]});
            var Q1;
            {var subQ0=sQuery(id+"F6.wireOp",EDGE,"E32.1.0");Q1=makeQuery(id+"F6.imprint","IMPRINT",FACE,{"disambiguationData":[TD([[makeQuery(id+"F6.imprint","IMPRINT",EDGE,{"derivedFrom":subQ0}),-1.0]])]});}
            var Q2;
            {var subQ0=sQuery(id+"F6.wireOp",EDGE,"E32.2.0");Q2=makeQuery(id+"F6.imprint","IMPRINT",FACE,{"disambiguationData":[TD([[makeQuery(id+"F6.imprint","IMPRINT",EDGE,{"derivedFrom":subQ0}),-1.0]])]});}
            var Q3;
            {var subQ0=sQuery(id+"F6.wireOp",EDGE,"E32.3.0");Q3=makeQuery(id+"F6.imprint","IMPRINT",FACE,{"disambiguationData":[TD([[makeQuery(id+"F6.imprint","IMPRINT",EDGE,{"derivedFrom":subQ0}),-1.0]])]});}
            extrude(context, id + "F7", {"entities" : qUnion([Q0, Q1, Q2, Q3]), "operationType" : NewBodyOperationType.REMOVE, "oppositeDirection" : true, "depth" : 54 * mm, "offsetDistance" : 25 * mm});
        }
    });
